# Revit family: KEUCO_53902010002
name_source: partatom
category: Sanitärinstallationen
revit_build: Autodesk Revit 2016 (Build: 20150220_1215(x64)
units: mm (PartAtom-declared; Revit-internal decimal feet)

## family parameters
Arbeitsebenenbasiert = Ja
Beim Laden mit Abzugskörper schneiden = Nein
Bemaßung runder Anschluss = Durchmesser verwenden
Gemeinsam genutzt = Nein
Immer vertikal = Ja
OmniClass-Nummer = 23.45.00.00
Raumberechnungspunkt = Nein
Teiletyp = Normal

## types (2) — shared parameters
Artikelnummer = 53902010002
Beschreibung = mit Zugstangen-Ablaufgarnitur 1 1/4 Zoll
Einlochmontage mit Schnell-Montage-System
Mischwasserkartusche mit keramischen Dichtscheiben
und Temperaturbegrenzung
Luftsprudler M 24x1, Strahlwinkel verstellbar +/- 8°
Druckschläuche 570 mm G 3/8 Zoll
Durchflussmenge begrenzt auf 6 l/min.
geräuschgeprüft
Hersteller = KEUCO
Kategorie = ARM
Preisgruppe = 1
URL = https://www.keuco.com
Verwendung = GWC / WP
Vorgabe-Ansicht = 1219 mm

## per-type parameters (varying)
| type | Ausschreibungstext | Gewicht | Material Wasserhahn |
| 53902010002 | KEUCO PLAN BLUE Einhebel-Waschtischmischer 130, 53902010002
hochglanzverchromter Einhebel-Waschtischmischer, 
in ästhetischem, funktionalem Design, 
für Standmontage, inklusive Zugstangen-Ablaufgarnitur,
hochwertige Mischwasserkartusche mit 
keramischen Dichtscheiben und Temperaturbegrenzung,
Durchflussmenge begrenzt auf 6 l/min.,
Betätigungselement aus Metall,
Einlochmontage mit Schnell-Montage-System 
für Waschtische, bzw. Waschtischplatten mit 
einer maximalen Stärke von 40 mm,
Luftsprudler M 24x1, Strahlwinkel verstellbar +/- 8°,
Höhe 204 mm, Auslaufhöhe 125 mm, Ausladung 162 mm,
Grundkörperdurchmesser 48 mm, Auslaufdurchmesser 28 mm
Wasseranschluss mit flexiblen Druckschläuchen, 
Länge 570 mm, Gewindedurchmesser G 3/8 Zoll,
Anschlussrohrlänge 350 mm,
Zugstangen-Ablaufgarnitur mit 
G 1 1/4 Zoll Anschlussgewinde,
Länge der Zugstange 400 mm,
Abdeckstopfen Durchmesser 63 mm | 858 | Chrome |
| 53902170002 | KEUCO PLAN BLUE Einhebel-Waschtischmischer 130, 53902170002
Einhebel-Waschtischmischer in Aluminium-finish, 
in ästhetischem, funktionalem Design, 
für Standmontage, inklusive Zugstangen-Ablaufgarnitur,
hochwertige Mischwasserkartusche mit 
keramischen Dichtscheiben und Temperaturbegrenzung,
Durchflussmenge begrenzt auf 6 l/min.,
Betätigungselement aus Metall,
Einlochmontage mit Schnell-Montage-System 
für Waschtische, bzw. Waschtischplatten mit 
einer maximalen Stärke von 40 mm,
Luftsprudler M 24x1, Strahlwinkel verstellbar +/- 8°,
Höhe 204 mm, Auslaufhöhe 125 mm, Ausladung 162 mm,
Grundkörperdurchmesser 48 mm, Auslaufdurchmesser 28 mm
Wasseranschluss mit flexiblen Druckschläuchen, 
Länge 570 mm, Gewindedurchmesser G 3/8 Zoll,
Anschlussrohrlänge 350 mm,
Zugstangen-Ablaufgarnitur mit 
G 1 1/4 Zoll Anschlussgewinde,
Länge der Zugstange 400 mm,
Abdeckstopfen Durchmesser 63 mm | 2844.6 | Aluminum |

## geometry (parser evidence)
native form markers: Sweep x1
no freeform markers — native parametric forms only
